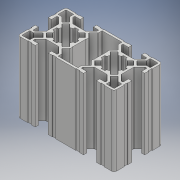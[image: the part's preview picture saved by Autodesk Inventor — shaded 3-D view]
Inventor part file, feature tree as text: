
AUTODESK INVENTOR PART (.ipt)
format: ipt  version: 2018 (Build 220112000, 112)  size: 577,024 bytes
history: native  units: mm
features: other x1, extrude x1, sketch x1
ambient origin geometry x8: Origin, YZ Plane, XZ Plane, XY Plane, X Axis, Y Axis, Z Axis, Center Point
bodies: Body1 (feature_tree)
feature tree (3):
  other  "Sólido1"
  extrude  "Extrusão1"  [1 undecoded]
  sketch  "Esboço1"  dims[d0=44.0mm d1=0.0mm]
note: 1 required parameter value undecoded (feature->parameter linkage not recoverable at this tier; creation-order binding heuristic only, values carry confidence <= 0.55)
